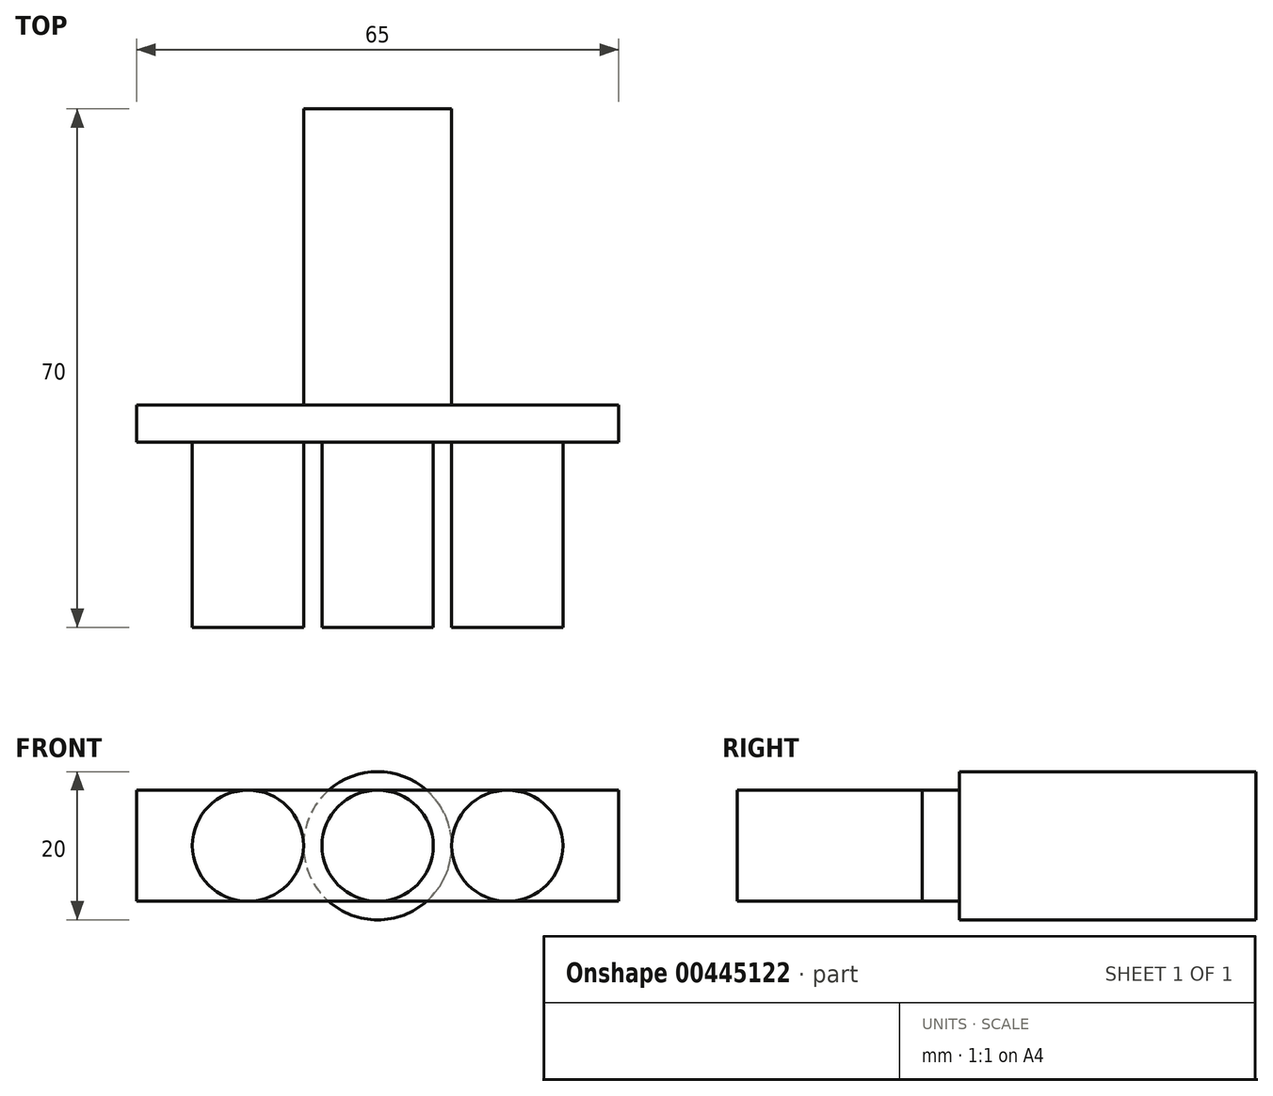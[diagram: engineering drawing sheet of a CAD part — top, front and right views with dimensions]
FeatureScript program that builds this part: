
annotation { "Feature Type Name" : "Feature", "Feature Type Description" : "" }
export const myFeature = defineFeature(function(context is Context, id is Id, definition is map)
    precondition{}
    {
        {
            var Q0;
            Q0=qCreatedBy(makeId("Front.planeOp"),FACE);
            var sketch = newSketch(context, id + "F0", { "sketchPlane" : qUnion([Q0])});
            skLineSegment(sketch, "E0.bottom", {"start": v(32.5, -7.5) * mm, "end": v(-32.5, -7.5) * mm});
            skLineSegment(sketch, "E0.top", {"start": v(32.5, 7.5) * mm, "end": v(-32.5, 7.5) * mm});
            skLineSegment(sketch, "E0.left", {"start": v(32.5, -7.5) * mm, "end": v(32.5, 7.5) * mm});
            skLineSegment(sketch, "E0.right", {"start": v(-32.5, -7.5) * mm, "end": v(-32.5, 7.5) * mm});
            skPoint(sketch, "E0.middle", {"position": v(0, 0) * mm});
            skCircle(sketch, "E1", {"center": v(0, 0) * mm, "radius": 7.5 * mm});
            skLineSegment(sketch, "E2", {"start": v(-7.5, 0) * mm, "end": v(-17.5, 0) * mm});
            skLineSegment(sketch, "E3", {"start": v(7.5, 0) * mm, "end": v(17.5, 0) * mm});
            skPoint(sketch, "E3.endSnap0", {"position": v(32.5, 0) * mm});
            skCircle(sketch, "E4", {"center": v(-17.5, 0) * mm, "radius": 7.5 * mm});
            skCircle(sketch, "E5", {"center": v(17.5, 0) * mm, "radius": 7.5 * mm});
            skSolve(sketch);
        }
        {
            var Q0;
            Q0 = qSketchRegion(id + "F0", true);
            extrude(context, id + "F1", {"entities" : qUnion([Q0]), "depth" : 5 * mm});
        }
        {
            var Q0;
            {var subQ0=sQuery(id+"F0.wireOp",EDGE,"E4");var subQ1=makeQuery(id+"F0.imprint","INTERSECT",VERTEX,{"derivedFrom":[sQuery(id+"F0.wireOp",EDGE,"E0.top"),subQ0]});Q0=makeQuery(id+"F0.imprint","IMPRINT",FACE,{"disambiguationData":[TD([[makeQuery(id+"F0.imprint","IMPRINT",EDGE,{"disambiguationData":[TD([[subQ1,1.0]])],"derivedFrom":subQ0}),1.0]])]});}
            var Q1;
            {var subQ0=sQuery(id+"F0.wireOp",EDGE,"E1");var subQ1=makeQuery(id+"F0.imprint","INTERSECT",VERTEX,{"derivedFrom":[subQ0,sQuery(id+"F0.wireOp",EDGE,"E3")]});Q1=makeQuery(id+"F0.imprint","IMPRINT",FACE,{"disambiguationData":[TD([[makeQuery(id+"F0.imprint","IMPRINT",EDGE,{"disambiguationData":[TD([[subQ1,-1.0]])],"derivedFrom":subQ0}),1.0]])]});}
            var Q2;
            {var subQ0=sQuery(id+"F0.wireOp",EDGE,"E5");var subQ1=makeQuery(id+"F0.imprint","INTERSECT",VERTEX,{"derivedFrom":[sQuery(id+"F0.wireOp",EDGE,"E0.top"),subQ0]});Q2=makeQuery(id+"F0.imprint","IMPRINT",FACE,{"disambiguationData":[TD([[makeQuery(id+"F0.imprint","IMPRINT",EDGE,{"disambiguationData":[TD([[subQ1,-1.0]])],"derivedFrom":subQ0}),1.0]])]});}
            extrude(context, id + "F2", {"entities" : qUnion([Q0, Q1, Q2]), "operationType" : NewBodyOperationType.ADD, "depth" : 30 * mm});
        }
        {
            var Q0;
            Q0=qCreatedBy(makeId("Front.planeOp"),FACE);
            var sketch = newSketch(context, id + "F3", { "sketchPlane" : qUnion([Q0])});
            skCircle(sketch, "E6", {"center": v(0, 0) * mm, "radius": 10 * mm});
            skSolve(sketch);
        }
        {
            var Q0;
            Q0=makeQuery(id+"F3.imprint","IMPRINT",FACE,{"disambiguationData":[TD([[makeQuery(id+"F3.imprint","IMPRINT",EDGE,{"derivedFrom":sQuery(id+"F3.wireOp",EDGE,"E6")}),1.0]])]});
            extrude(context, id + "F4", {"entities" : qUnion([Q0]), "operationType" : NewBodyOperationType.ADD, "oppositeDirection" : true, "depth" : 40 * mm});
        }
    });
